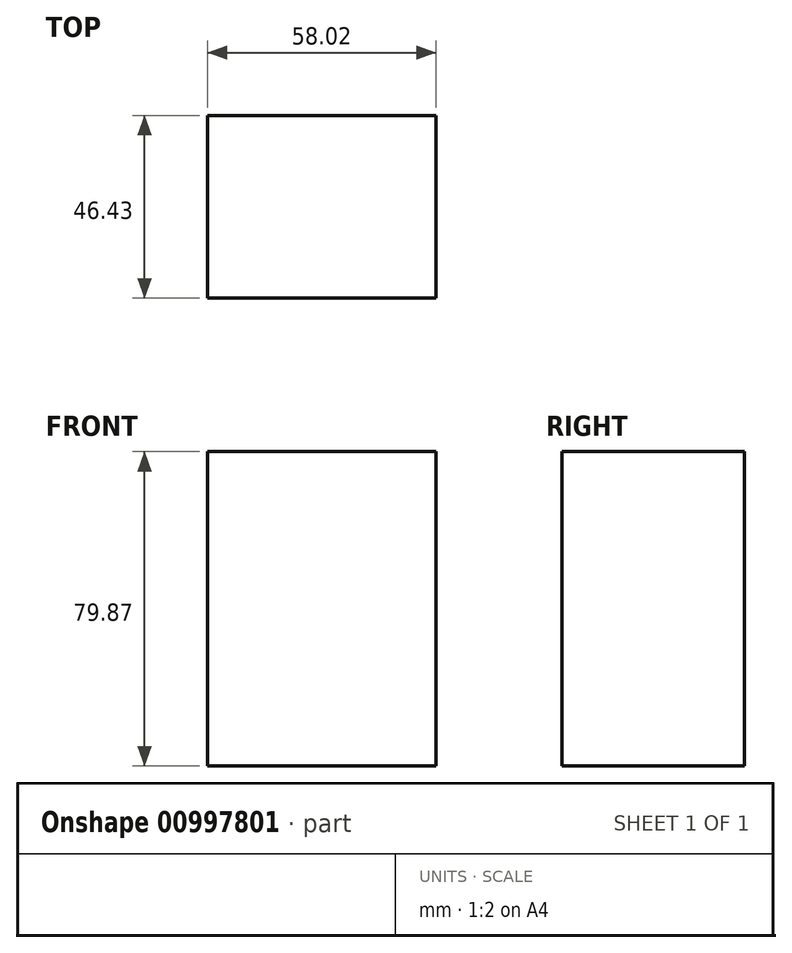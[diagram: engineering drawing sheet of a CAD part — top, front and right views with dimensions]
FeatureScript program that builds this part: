
annotation { "Feature Type Name" : "Feature", "Feature Type Description" : "" }
export const myFeature = defineFeature(function(context is Context, id is Id, definition is map)
    precondition{}
    {
        {
            var Q0;
            Q0=qCreatedBy(makeId("Front.planeOp"),FACE);
            var sketch = newSketch(context, id + "F0", { "sketchPlane" : qUnion([Q0])});
            skLineSegment(sketch, "E0.bottom", {"start": v(-34.37, 21.16) * mm, "end": v(23.65, 21.16) * mm});
            skLineSegment(sketch, "E0.top", {"start": v(-34.37, -58.71) * mm, "end": v(23.65, -58.71) * mm});
            skLineSegment(sketch, "E0.left", {"start": v(-34.37, 21.16) * mm, "end": v(-34.37, -58.71) * mm});
            skLineSegment(sketch, "E0.right", {"start": v(23.65, 21.16) * mm, "end": v(23.65, -58.71) * mm});
            skSolve(sketch);
        }
        {
            var Q0;
            Q0=makeQuery(id+"F0.imprint","IMPRINT",FACE,{"disambiguationData":[TD([[makeQuery(id+"F0.imprint","IMPRINT",EDGE,{"derivedFrom":sQuery(id+"F0.wireOp",EDGE,"E0.bottom")}),-1.0]])]});
            extrude(context, id + "F1", {"entities" : qUnion([Q0]), "depth" : 46.43 * mm, "offsetDistance" : 25.4 * mm});
        }
    });
